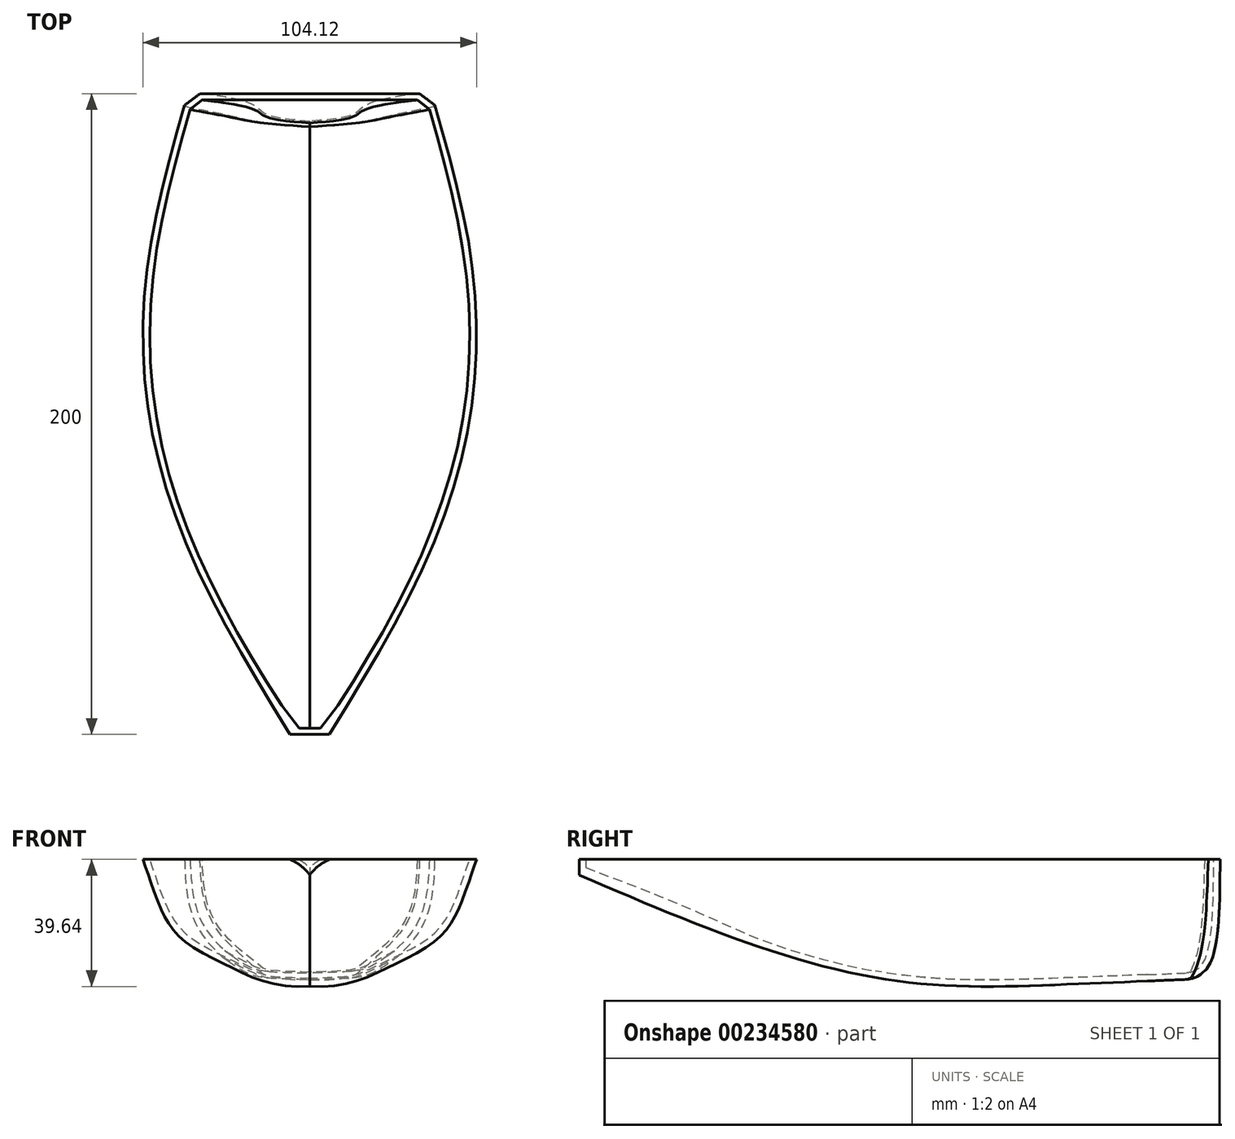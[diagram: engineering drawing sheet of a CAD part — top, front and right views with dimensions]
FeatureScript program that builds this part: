
annotation { "Feature Type Name" : "Feature", "Feature Type Description" : "" }
export const myFeature = defineFeature(function(context is Context, id is Id, definition is map)
    precondition{}
    {
        {
            var Q0;
            Q0=qCreatedBy(makeId("Front.planeOp"),FACE);
            var sketch = newSketch(context, id + "F0", { "sketchPlane" : qUnion([Q0])});
            skLineSegment(sketch, "E0", {"start": v(0, 0) * mm, "end": v(-38, 0) * mm});
            skFitSpline(sketch, "E1", {"points": [v(-38, 0) * mm, v(-32.6, -23.87) * mm, v(-19.8, -35.62) * mm, v(0, -37) * mm], "startDerivative": vector(-0.53, -88.18) * mm, "endDerivative": vector(129.21, -5.25) * mm});
            skLineSegment(sketch, "E2", {"start": v(0, 0) * mm, "end": v(0, -37) * mm});
            skSolve(sketch);
        }
        {
            var Q0;
            Q0=qCreatedBy(makeId("Front.planeOp"),FACE);
            cPlane(context, id + "F1", {"entities" : qUnion([Q0]), "cplaneType" : CPlaneType.OFFSET, "offset" : 50 * mm, "width" : 150 * mm, "height" : 150 * mm});
        }
        {
            var Q0;
            Q0=qCreatedBy(id+"F1.planeOp",FACE);
            cPlane(context, id + "F2", {"entities" : qUnion([Q0]), "cplaneType" : CPlaneType.OFFSET, "offset" : 50 * mm, "width" : 150 * mm, "height" : 150 * mm});
        }
        {
            var Q0;
            Q0=qCreatedBy(id+"F2.planeOp",FACE);
            cPlane(context, id + "F3", {"entities" : qUnion([Q0]), "cplaneType" : CPlaneType.OFFSET, "offset" : 50 * mm, "width" : 150 * mm, "height" : 150 * mm});
        }
        {
            var Q0;
            Q0=qCreatedBy(id+"F3.planeOp",FACE);
            cPlane(context, id + "F4", {"entities" : qUnion([Q0]), "cplaneType" : CPlaneType.OFFSET, "offset" : 50 * mm, "width" : 150 * mm, "height" : 150 * mm});
        }
        {
            var Q0;
            Q0=qCreatedBy(id+"F1.planeOp",FACE);
            var sketch = newSketch(context, id + "F5", { "sketchPlane" : qUnion([Q0])});
            skLineSegment(sketch, "E3", {"start": v(0, 0) * mm, "end": v(-50.12, 0) * mm});
            skFitSpline(sketch, "E4", {"points": [v(-50.12, 0) * mm, v(-40.34, -22.27) * mm, v(-23.93, -32.46) * mm, v(0, -39) * mm], "startDerivative": vector(31, -92.9) * mm, "endDerivative": vector(95.73, 5.08) * mm});
            skLineSegment(sketch, "E5", {"start": v(0, -39) * mm, "end": v(0, 0) * mm});
            skSolve(sketch);
        }
        {
            var Q0;
            Q0=qCreatedBy(id+"F2.planeOp",FACE);
            var sketch = newSketch(context, id + "F6", { "sketchPlane" : qUnion([Q0])});
            skLineSegment(sketch, "E6", {"start": v(0, 0) * mm, "end": v(-50.17, 0) * mm});
            skFitSpline(sketch, "E7", {"points": [v(-50.17, 0) * mm, v(-40.2, -22.32) * mm, v(-22.89, -32.8) * mm, v(0, -38) * mm], "startDerivative": vector(25.45, -76.64) * mm, "endDerivative": vector(99.64, 2.91) * mm});
            skLineSegment(sketch, "E8", {"start": v(0, 0) * mm, "end": v(0, -38) * mm});
            skSolve(sketch);
        }
        {
            var Q0;
            Q0=qCreatedBy(id+"F3.planeOp",FACE);
            var sketch = newSketch(context, id + "F7", { "sketchPlane" : qUnion([Q0])});
            skLineSegment(sketch, "E9", {"start": v(0, 0) * mm, "end": v(-34.38, 0) * mm});
            skFitSpline(sketch, "E10", {"points": [v(-34.38, 0) * mm, v(-26.81, -12.4) * mm, v(-5.31, -21.39) * mm, v(0, -25.12) * mm], "startDerivative": vector(13.41, -39.8) * mm, "endDerivative": vector(16.82, -16.35) * mm});
            skLineSegment(sketch, "E11", {"start": v(0, 0) * mm, "end": v(0, -25.12) * mm});
            skSolve(sketch);
        }
        {
            var Q0;
            Q0=qCreatedBy(id+"F4.planeOp",FACE);
            var sketch = newSketch(context, id + "F8", { "sketchPlane" : qUnion([Q0])});
            skLineSegment(sketch, "E12", {"start": v(0, 0) * mm, "end": v(-6.14, 0) * mm});
            skFitSpline(sketch, "E13", {"points": [v(-6.14, 0) * mm, v(-2.75, -1.97) * mm, v(0, -4.84) * mm], "startDerivative": vector(7.14, -3.51) * mm, "endDerivative": vector(5.15, -6.16) * mm});
            skLineSegment(sketch, "E14", {"start": v(0, 0) * mm, "end": v(0, -4.84) * mm});
            skSolve(sketch);
        }
        {
            var Q0;
            Q0=makeQuery(id+"F0.imprint","IMPRINT",FACE,{"disambiguationData":[TD([[makeQuery(id+"F0.imprint","IMPRINT",EDGE,{"derivedFrom":sQuery(id+"F0.wireOp",EDGE,"E0")}),1.0]])]});
            var Q1;
            Q1=makeQuery(id+"F5.imprint","IMPRINT",FACE,{"disambiguationData":[TD([[makeQuery(id+"F5.imprint","IMPRINT",EDGE,{"derivedFrom":sQuery(id+"F5.wireOp",EDGE,"E3")}),1.0]])]});
            var Q2;
            Q2=makeQuery(id+"F6.imprint","IMPRINT",FACE,{"disambiguationData":[TD([[makeQuery(id+"F6.imprint","IMPRINT",EDGE,{"derivedFrom":sQuery(id+"F6.wireOp",EDGE,"E6")}),1.0]])]});
            var Q3;
            Q3=makeQuery(id+"F7.imprint","IMPRINT",FACE,{"disambiguationData":[TD([[makeQuery(id+"F7.imprint","IMPRINT",EDGE,{"derivedFrom":sQuery(id+"F7.wireOp",EDGE,"E9")}),1.0]])]});
            var Q4;
            Q4=makeQuery(id+"F8.imprint","IMPRINT",FACE,{"disambiguationData":[TD([[makeQuery(id+"F8.imprint","IMPRINT",EDGE,{"derivedFrom":sQuery(id+"F8.wireOp",EDGE,"E12")}),1.0]])]});
            loft(context, id + "F9", {"sheetProfilesArray" : [{ "sheetProfileEntities" : qUnion([Q0]) }, { "sheetProfileEntities" : qUnion([Q1]) }, { "sheetProfileEntities" : qUnion([Q2]) }, { "sheetProfileEntities" : qUnion([Q3]) }, { "sheetProfileEntities" : qUnion([Q4]) }]});
        }
        {
            var Q0;
            Q0=makeQuery(id+"F9.opLoft","SWEPT_BODY",BODY,{"disambiguationData":[OSD([makeQuery(id+"F0.imprint","IMPRINT",FACE,{"disambiguationData":[TD([[makeQuery(id+"F0.imprint","IMPRINT",EDGE,{"derivedFrom":sQuery(id+"F0.wireOp",EDGE,"E0")}),1.0]])]}),sQuery(id+"F5.wireOp",EDGE,"E5"),sQuery(id+"F6.wireOp",EDGE,"E6"),sQuery(id+"F7.wireOp",EDGE,"E9"),makeQuery(id+"F8.imprint","IMPRINT",FACE,{"disambiguationData":[TD([[makeQuery(id+"F8.imprint","IMPRINT",EDGE,{"derivedFrom":sQuery(id+"F8.wireOp",EDGE,"E12")}),1.0]])]})])]});
            var Q1;
            Q1=qCreatedBy(makeId("Right.planeOp"),FACE);
            mirror(context, id + "F10", {"operationType" : NewBodyOperationType.ADD, "entities" : qUnion([Q0]), "mirrorPlane" : qUnion([Q1])});
        }
        {
            var Q0;
            Q0=qCreatedBy(makeId("Right.planeOp"),FACE);
            var sketch = newSketch(context, id + "F11", { "sketchPlane" : qUnion([Q0])});
            skLineSegment(sketch, "E15", {"start": v(0, 4.26) * mm, "end": v(0, -38.74) * mm});
            skLineSegment(sketch, "E16", {"start": v(0, -38.74) * mm, "end": v(-13, -38.74) * mm});
            skFitSpline(sketch, "E17", {"points": [v(-13, -38.74) * mm, v(-4.3, -34.4) * mm, v(0, 0) * mm], "startDerivative": vector(31.36, 13.7) * mm, "endDerivative": vector(0, 79.1) * mm});
            skSolve(sketch);
        }
        {
            var Q0;
            Q0 = qSketchRegion(id + "F11", true);
            extrude(context, id + "F12", {"entities" : qUnion([Q0]), "operationType" : NewBodyOperationType.REMOVE, "endBound" : BoundingType.SYMMETRIC, "oppositeDirection" : true, "depth" : 85 * mm});
        }
        {
            var Q0;
            {var subQ0=sQuery(id+"F5.wireOp",EDGE,"E4");var subQ1=sQuery(id+"F5.wireOp",EDGE,"E5");var subQ2=sQuery(id+"F5.wireOp",EDGE,"E3");var subQ3=sQuery(id+"F0.wireOp",EDGE,"E1");var subQ4=sQuery(id+"F0.wireOp",EDGE,"E2");var subQ5=sQuery(id+"F0.wireOp",EDGE,"E0");Q0=makeQuery(id+"F12.boolean.opBoolean","INTERSECT",EDGE,{"derivedFrom":[makeQuery(id+"F9.opLoft","SWEPT_FACE",FACE,{"disambiguationData":[OSD([subQ5,subQ3,subQ4,subQ2,subQ0,subQ1]),TDD([makeQuery(id+"F0.imprint","INTERSECT",VERTEX,{"derivedFrom":[subQ5,subQ3]}),makeQuery(id+"F0.imprint","INTERSECT",VERTEX,{"derivedFrom":[subQ3,subQ4]}),makeQuery(id+"F0.imprint","IMPRINT",EDGE,{"derivedFrom":subQ3}),makeQuery(id+"F5.imprint","INTERSECT",VERTEX,{"derivedFrom":[subQ2,subQ0]}),makeQuery(id+"F5.imprint","INTERSECT",VERTEX,{"derivedFrom":[subQ0,subQ1]}),makeQuery(id+"F5.imprint","IMPRINT",EDGE,{"derivedFrom":subQ0})])]}),makeQuery(id+"F12.opExtrude","SWEPT_FACE",FACE,{"disambiguationData":[OSD([sQuery(id+"F11.wireOp",EDGE,"E17")])]})]});}
            var Q1;
            {var subQ0=sQuery(id+"F5.wireOp",EDGE,"E4");var subQ1=sQuery(id+"F5.wireOp",EDGE,"E5");var subQ2=sQuery(id+"F5.wireOp",EDGE,"E3");var subQ3=sQuery(id+"F0.wireOp",EDGE,"E1");var subQ4=sQuery(id+"F0.wireOp",EDGE,"E2");var subQ5=sQuery(id+"F0.wireOp",EDGE,"E0");Q1=makeQuery(id+"F12.boolean.opBoolean","INTERSECT",EDGE,{"derivedFrom":[makeQuery(id+"F10.opPattern","COPY",FACE,{"derivedFrom":makeQuery(id+"F9.opLoft","SWEPT_FACE",FACE,{"disambiguationData":[OSD([subQ5,subQ3,subQ4,subQ2,subQ0,subQ1]),TDD([makeQuery(id+"F0.imprint","INTERSECT",VERTEX,{"derivedFrom":[subQ5,subQ3]}),makeQuery(id+"F0.imprint","INTERSECT",VERTEX,{"derivedFrom":[subQ3,subQ4]}),makeQuery(id+"F0.imprint","IMPRINT",EDGE,{"derivedFrom":subQ3}),makeQuery(id+"F5.imprint","INTERSECT",VERTEX,{"derivedFrom":[subQ2,subQ0]}),makeQuery(id+"F5.imprint","INTERSECT",VERTEX,{"derivedFrom":[subQ0,subQ1]}),makeQuery(id+"F5.imprint","IMPRINT",EDGE,{"derivedFrom":subQ0})])]}),"instanceName":"1"}),makeQuery(id+"F12.opExtrude","SWEPT_FACE",FACE,{"disambiguationData":[OSD([sQuery(id+"F11.wireOp",EDGE,"E17")])]})]});}
            chamfer(context, id + "F13", {"entities" : qUnion([Q0, Q1]), "width" : 5 * mm, "tangentPropagation" : true});
        }
        {
            var Q0;
            {var subQ0=sQuery(id+"F5.wireOp",EDGE,"E3");var subQ1=sQuery(id+"F5.wireOp",EDGE,"E4");var subQ2=sQuery(id+"F5.wireOp",EDGE,"E5");var subQ3=sQuery(id+"F0.wireOp",EDGE,"E0");var subQ4=sQuery(id+"F0.wireOp",EDGE,"E1");var subQ5=sQuery(id+"F0.wireOp",EDGE,"E2");var subQ6=makeQuery(id+"F9.opLoft","SWEPT_FACE",FACE,{"disambiguationData":[OSD([subQ3,subQ4,subQ5,subQ0,subQ1,subQ2]),TDD([makeQuery(id+"F0.imprint","INTERSECT",VERTEX,{"derivedFrom":[subQ3,subQ5]}),makeQuery(id+"F0.imprint","INTERSECT",VERTEX,{"derivedFrom":[subQ3,subQ4]}),makeQuery(id+"F0.imprint","IMPRINT",EDGE,{"derivedFrom":subQ3}),makeQuery(id+"F5.imprint","INTERSECT",VERTEX,{"derivedFrom":[subQ0,subQ2]}),makeQuery(id+"F5.imprint","INTERSECT",VERTEX,{"derivedFrom":[subQ0,subQ1]}),makeQuery(id+"F5.imprint","IMPRINT",EDGE,{"derivedFrom":subQ0})])]});Q0=makeQuery(id+"F10.boolean.opBoolean","MERGE",FACE,{"derivedFrom":[subQ6,makeQuery(id+"F10.opPattern","COPY",FACE,{"derivedFrom":subQ6,"instanceName":"1"})]});}
            shell(context, id + "F14", {"entities" : qUnion([Q0]), "thickness" : 2 * mm});
        }
    });
